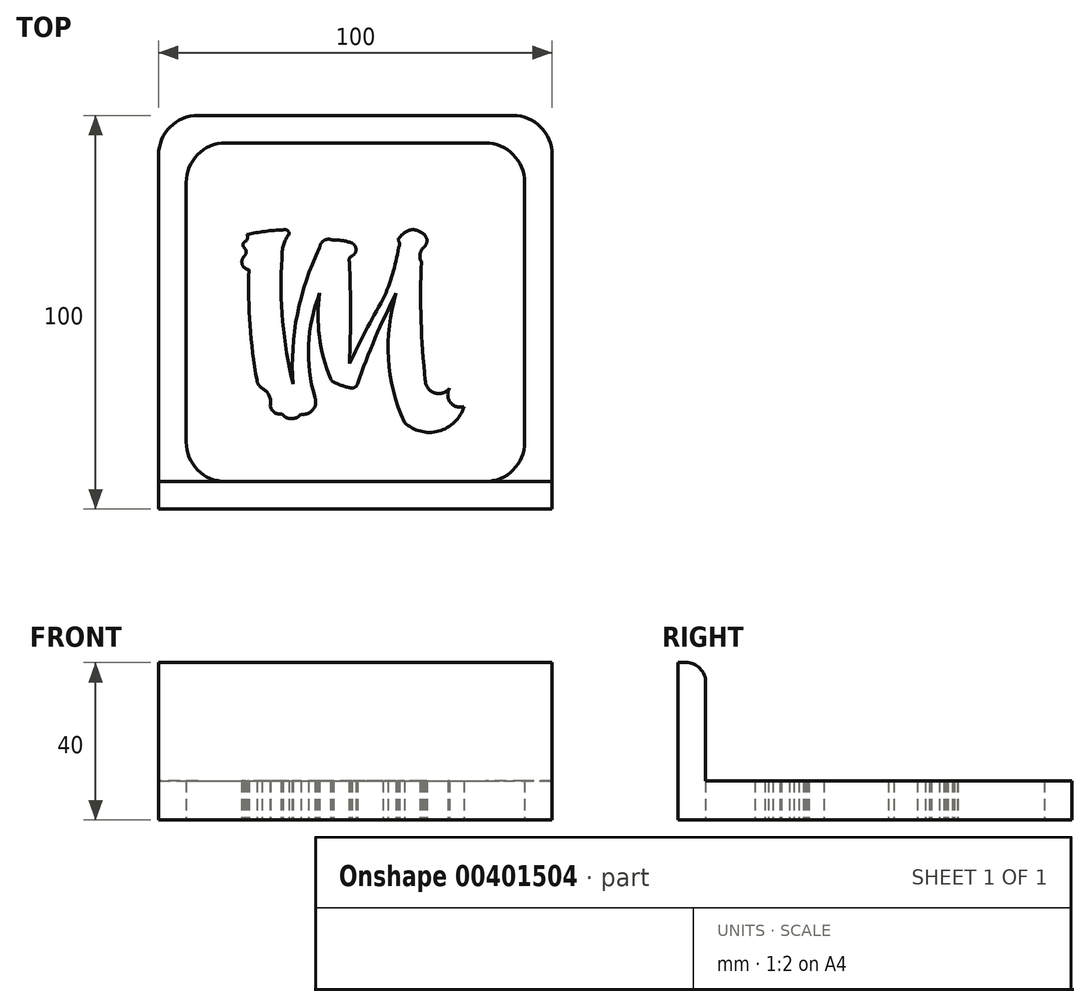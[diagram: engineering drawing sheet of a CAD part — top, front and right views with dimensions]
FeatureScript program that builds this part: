
annotation { "Feature Type Name" : "Feature", "Feature Type Description" : "" }
export const myFeature = defineFeature(function(context is Context, id is Id, definition is map)
    precondition{}
    {
        {
            var Q0;
            Q0=qCreatedBy(makeId("Top.planeOp"),FACE);
            var sketch = newSketch(context, id + "F0", { "sketchPlane" : qUnion([Q0])});
            skLineSegment(sketch, "E0.bottom", {"start": v(0, 0) * mm, "end": v(100, 0) * mm});
            skLineSegment(sketch, "E0.top", {"start": v(0, 100) * mm, "end": v(100, 100) * mm});
            skLineSegment(sketch, "E0.left", {"start": v(0, 0) * mm, "end": v(0, 100) * mm});
            skLineSegment(sketch, "E0.right", {"start": v(100, 0) * mm, "end": v(100, 100) * mm});
            skLineSegment(sketch, "E1.bottom", {"start": v(7, 7) * mm, "end": v(93, 7) * mm});
            skLineSegment(sketch, "E1.top", {"start": v(7, 93) * mm, "end": v(93, 93) * mm});
            skLineSegment(sketch, "E1.left", {"start": v(7, 7) * mm, "end": v(7, 93) * mm});
            skLineSegment(sketch, "E1.right", {"start": v(93, 7) * mm, "end": v(93, 93) * mm});
            skArc(sketch, "E2", {"start": v(33.2, 70.01) * mm, "mid": v(31.73, 67.08) * mm, "end": v(31.33, 63.82) * mm});
            skArc(sketch, "E3", {"start": v(31.33, 63.82) * mm, "mid": v(31.53, 47.7) * mm, "end": v(34.1, 31.78) * mm});
            skArc(sketch, "E4", {"start": v(40.94, 66.39) * mm, "mid": v(35.26, 49.53) * mm, "end": v(34.1, 31.78) * mm});
            skArc(sketch, "E5", {"start": v(44.05, 68.4) * mm, "mid": v(41.96, 68.2) * mm, "end": v(40.94, 66.39) * mm});
            skArc(sketch, "E6", {"start": v(49.12, 67.57) * mm, "mid": v(46.62, 68.22) * mm, "end": v(44.05, 68.4) * mm});
            skArc(sketch, "E7", {"start": v(49.12, 64.3) * mm, "mid": v(50.15, 65.93) * mm, "end": v(49.12, 67.57) * mm});
            skArc(sketch, "E8", {"start": v(49.12, 64.3) * mm, "mid": v(48.48, 63.7) * mm, "end": v(48.47, 62.82) * mm});
            skArc(sketch, "E9", {"start": v(48.47, 37) * mm, "mid": v(48.76, 49.9) * mm, "end": v(48.47, 62.82) * mm});
            skArc(sketch, "E10", {"start": v(57.05, 53.38) * mm, "mid": v(52.61, 45.26) * mm, "end": v(48.47, 37) * mm});
            skArc(sketch, "E11", {"start": v(57.05, 53.38) * mm, "mid": v(59.46, 59.74) * mm, "end": v(60.95, 66.39) * mm});
            skArc(sketch, "E12", {"start": v(60.95, 66.39) * mm, "mid": v(61.2, 67.42) * mm, "end": v(60.75, 68.4) * mm});
            skArc(sketch, "E13", {"start": v(62.47, 70.21) * mm, "mid": v(61.55, 69.36) * mm, "end": v(60.75, 68.4) * mm});
            skArc(sketch, "E14", {"start": v(66.76, 70.21) * mm, "mid": v(64.61, 70.97) * mm, "end": v(62.47, 70.21) * mm});
            skArc(sketch, "E15", {"start": v(67.26, 66.39) * mm, "mid": v(68.16, 68.45) * mm, "end": v(66.76, 70.21) * mm});
            skArc(sketch, "E16", {"start": v(67.26, 66.39) * mm, "mid": v(66.4, 64.69) * mm, "end": v(66.74, 62.82) * mm});
            skArc(sketch, "E17", {"start": v(66.74, 62.82) * mm, "mid": v(66.69, 47.77) * mm, "end": v(67.74, 32.75) * mm});
            skArc(sketch, "E18", {"start": v(67.74, 32.75) * mm, "mid": v(70.13, 29.52) * mm, "end": v(73.97, 30.72) * mm});
            skArc(sketch, "E19", {"start": v(73.97, 30.72) * mm, "mid": v(74.12, 27.11) * mm, "end": v(77.56, 26.04) * mm});
            skArc(sketch, "E20", {"start": v(62.47, 22.05) * mm, "mid": v(71.14, 19.79) * mm, "end": v(77.56, 26.04) * mm});
            skArc(sketch, "E21", {"start": v(60.38, 54.83) * mm, "mid": v(58.4, 38.25) * mm, "end": v(62.47, 22.05) * mm});
            skArc(sketch, "E22", {"start": v(60.38, 54.83) * mm, "mid": v(55.03, 43.5) * mm, "end": v(50.55, 31.78) * mm});
            skArc(sketch, "E23", {"start": v(49.12, 30.72) * mm, "mid": v(50, 31.04) * mm, "end": v(50.55, 31.78) * mm});
            skArc(sketch, "E24", {"start": v(44.46, 32.3) * mm, "mid": v(46.73, 31.33) * mm, "end": v(49.12, 30.72) * mm});
            skArc(sketch, "E25", {"start": v(43.7, 33.19) * mm, "mid": v(43.97, 32.65) * mm, "end": v(44.46, 32.3) * mm});
            skArc(sketch, "E26", {"start": v(40.94, 54.83) * mm, "mid": v(40.84, 43.82) * mm, "end": v(43.7, 33.19) * mm});
            skArc(sketch, "E27", {"start": v(40.94, 54.83) * mm, "mid": v(38.08, 41.63) * mm, "end": v(39.78, 28.24) * mm});
            skArc(sketch, "E28", {"start": v(36.23, 24.12) * mm, "mid": v(39.18, 25.17) * mm, "end": v(39.78, 28.24) * mm});
            skArc(sketch, "E29", {"start": v(31.33, 24.12) * mm, "mid": v(33.78, 22.96) * mm, "end": v(36.23, 24.12) * mm});
            skArc(sketch, "E30", {"start": v(28.36, 26.2) * mm, "mid": v(29.44, 24.58) * mm, "end": v(31.33, 24.12) * mm});
            skArc(sketch, "E31", {"start": v(28.36, 26.2) * mm, "mid": v(28.1, 28.84) * mm, "end": v(26.24, 30.72) * mm});
            skArc(sketch, "E32", {"start": v(24.97, 32.75) * mm, "mid": v(25.35, 31.58) * mm, "end": v(26.24, 30.72) * mm});
            skArc(sketch, "E33", {"start": v(22.98, 60.8) * mm, "mid": v(23.22, 46.72) * mm, "end": v(24.97, 32.75) * mm});
            skArc(sketch, "E34", {"start": v(21.77, 64.3) * mm, "mid": v(21.25, 62.16) * mm, "end": v(22.98, 60.8) * mm});
            skArc(sketch, "E35", {"start": v(21.77, 64.3) * mm, "mid": v(22.24, 65.34) * mm, "end": v(21.77, 66.39) * mm});
            skArc(sketch, "E36", {"start": v(22.13, 68.03) * mm, "mid": v(21.46, 67.32) * mm, "end": v(21.77, 66.39) * mm});
            skArc(sketch, "E37", {"start": v(22.13, 68.03) * mm, "mid": v(22.6, 68.8) * mm, "end": v(22.49, 69.7) * mm});
            skArc(sketch, "E38", {"start": v(31.68, 70.94) * mm, "mid": v(27.05, 70.57) * mm, "end": v(22.49, 69.7) * mm});
            skArc(sketch, "E39", {"start": v(33.2, 70.01) * mm, "mid": v(32.67, 70.85) * mm, "end": v(31.68, 70.94) * mm});
            skSolve(sketch);
        }
        {
            var Q0;
            Q0 = qSketchRegion(id + "F0", true);
            var Q1;
            Q1=makeQuery(id+"F0.imprint","IMPRINT",FACE,{"disambiguationData":[TD([[makeQuery(id+"F0.imprint","IMPRINT",EDGE,{"derivedFrom":sQuery(id+"F0.wireOp",EDGE,"E2")}),-1.0]])]});
            extrude(context, id + "F1", {"entities" : qUnion([Q0, Q1]), "depth" : 10 * mm});
        }
        {
            var Q0;
            Q0=makeQuery(id+"F1.opExtrude","CAP_FACE",FACE,{"disambiguationData":[OSD([sQuery(id+"F0.wireOp",EDGE,"E0.bottom"),sQuery(id+"F0.wireOp",EDGE,"E0.top"),sQuery(id+"F0.wireOp",EDGE,"E0.left"),sQuery(id+"F0.wireOp",EDGE,"E0.right"),sQuery(id+"F0.wireOp",EDGE,"E1.bottom"),sQuery(id+"F0.wireOp",EDGE,"E1.top"),sQuery(id+"F0.wireOp",EDGE,"E1.left"),sQuery(id+"F0.wireOp",EDGE,"E1.right")])],"isStart":false});
            var sketch = newSketch(context, id + "F2", { "sketchPlane" : qUnion([Q0])});
            skLineSegment(sketch, "E40.bottom", {"start": v(0, 0) * mm, "end": v(100, 0) * mm});
            skLineSegment(sketch, "E40.top", {"start": v(0, 7) * mm, "end": v(100, 7) * mm});
            skLineSegment(sketch, "E40.left", {"start": v(0, 0) * mm, "end": v(0, 7) * mm});
            skLineSegment(sketch, "E40.right", {"start": v(100, 0) * mm, "end": v(100, 7) * mm});
            skSolve(sketch);
        }
        {
            var Q0;
            Q0 = qSketchRegion(id + "F2", true);
            extrude(context, id + "F3", {"entities" : qUnion([Q0]), "operationType" : NewBodyOperationType.ADD, "depth" : 30 * mm});
        }
        {
            var Q0;
            Q0=makeQuery(id+"F1.opExtrude","SWEPT_EDGE",EDGE,{"disambiguationData":[OSD([sQuery(id+"F0.wireOp",EDGE,"E0.top"),sQuery(id+"F0.wireOp",EDGE,"E0.left")])]});
            var Q1;
            Q1=makeQuery(id+"F1.opExtrude","SWEPT_EDGE",EDGE,{"disambiguationData":[OSD([sQuery(id+"F0.wireOp",EDGE,"E0.top"),sQuery(id+"F0.wireOp",EDGE,"E0.right")])]});
            var Q2;
            Q2=makeQuery(id+"F1.opExtrude","SWEPT_EDGE",EDGE,{"disambiguationData":[OSD([sQuery(id+"F0.wireOp",EDGE,"E1.bottom"),sQuery(id+"F0.wireOp",EDGE,"E1.left")])]});
            var Q3;
            Q3=makeQuery(id+"F1.opExtrude","SWEPT_EDGE",EDGE,{"disambiguationData":[OSD([sQuery(id+"F0.wireOp",EDGE,"E1.bottom"),sQuery(id+"F0.wireOp",EDGE,"E1.right")])]});
            var Q4;
            Q4=makeQuery(id+"F1.opExtrude","SWEPT_EDGE",EDGE,{"disambiguationData":[OSD([sQuery(id+"F0.wireOp",EDGE,"E1.top"),sQuery(id+"F0.wireOp",EDGE,"E1.right")])]});
            var Q5;
            Q5=makeQuery(id+"F1.opExtrude","SWEPT_EDGE",EDGE,{"disambiguationData":[OSD([sQuery(id+"F0.wireOp",EDGE,"E1.top"),sQuery(id+"F0.wireOp",EDGE,"E1.left")])]});
            fillet(context, id + "F4", {"entities" : qUnion([Q0, Q1, Q2, Q3, Q4, Q5]), "radius" : 10 * mm, "tangentPropagation" : true, "allowEdgeOverflow" : false});
        }
        {
            var Q0;
            Q0=makeQuery(id+"F3.opExtrude","CAP_EDGE",EDGE,{"disambiguationData":[OSD([sQuery(id+"F2.wireOp",EDGE,"E40.top")])],"isStart":false});
            fillet(context, id + "F5", {"entities" : qUnion([Q0]), "radius" : 5 * mm, "tangentPropagation" : true, "allowEdgeOverflow" : false});
        }
    });
